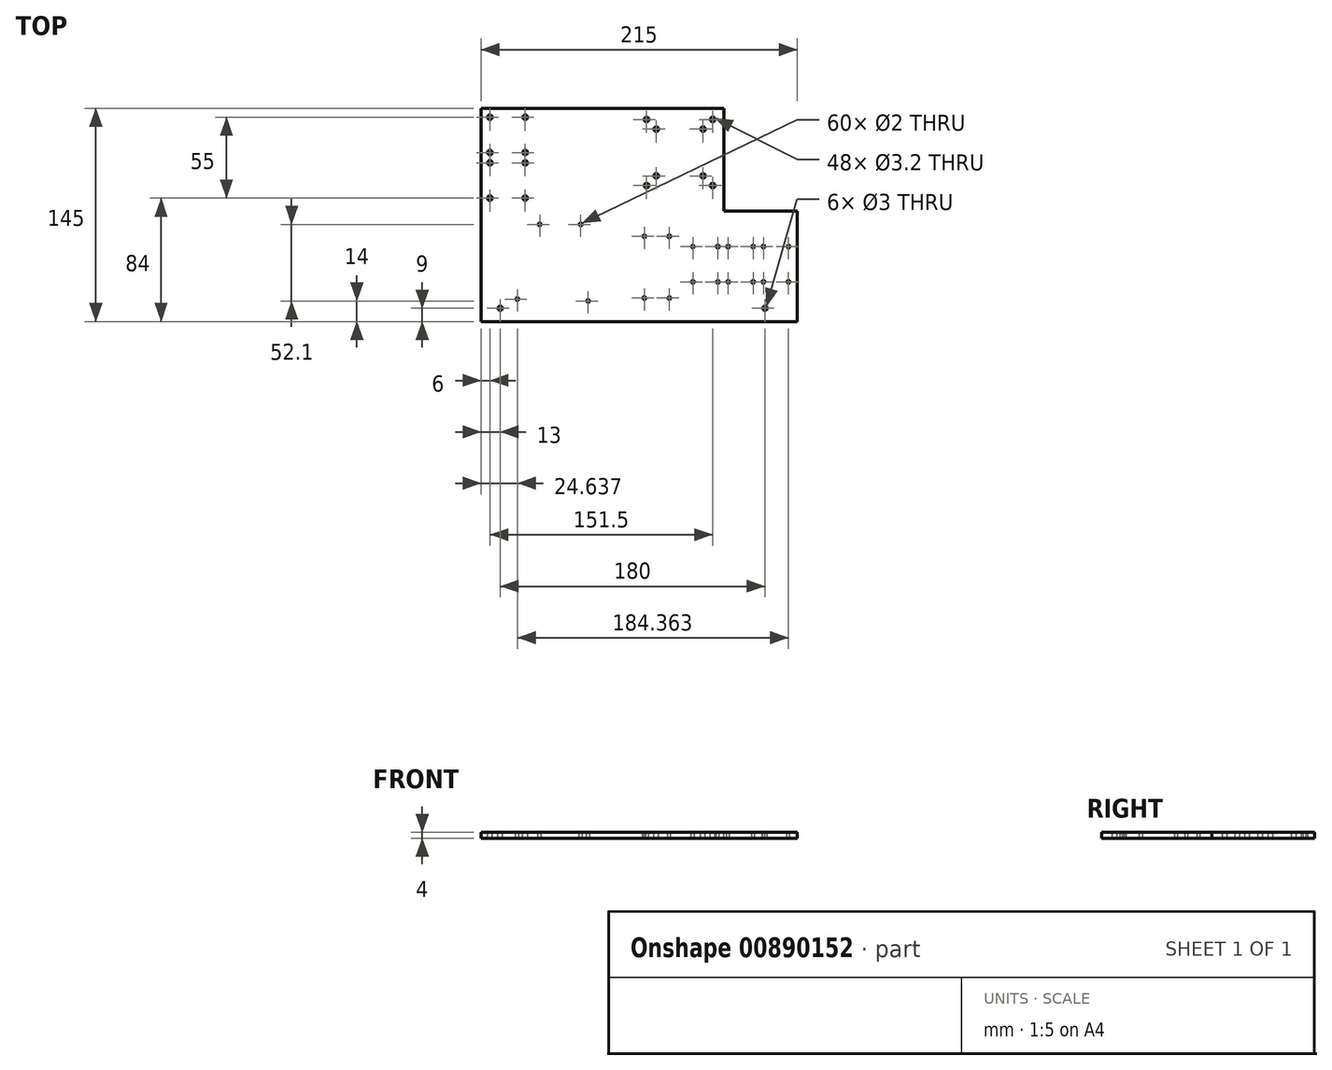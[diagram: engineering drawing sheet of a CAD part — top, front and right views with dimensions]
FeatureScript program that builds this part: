
annotation { "Feature Type Name" : "Feature", "Feature Type Description" : "" }
export const myFeature = defineFeature(function(context is Context, id is Id, definition is map)
    precondition{}
    {
        {
            var Q0;
            Q0=qCreatedBy(makeId("Top.planeOp"),FACE);
            var sketch = newSketch(context, id + "F0", { "sketchPlane" : qUnion([Q0])});
            skLineSegment(sketch, "E0.bottom", {"start": v(-107.5, 72.5) * mm, "end": v(107.5, 72.5) * mm});
            skLineSegment(sketch, "E0.top", {"start": v(-107.5, -72.5) * mm, "end": v(107.5, -72.5) * mm});
            skLineSegment(sketch, "E0.left", {"start": v(-107.5, 72.5) * mm, "end": v(-107.5, -72.5) * mm});
            skLineSegment(sketch, "E0.right", {"start": v(107.5, 72.5) * mm, "end": v(107.5, -72.5) * mm});
            skSolve(sketch);
        }
        {
            var Q0;
            Q0 = qSketchRegion(id + "F0", true);
            extrude(context, id + "F1", {"entities" : qUnion([Q0]), "depth" : 4 * mm, "offsetDistance" : 25 * mm});
        }
        {
            var Q0;
            Q0=makeQuery(id+"F1.opExtrude","CAP_FACE",FACE,{"disambiguationData":[OSD([sQuery(id+"F0.wireOp",EDGE,"E0.bottom"),sQuery(id+"F0.wireOp",EDGE,"E0.top"),sQuery(id+"F0.wireOp",EDGE,"E0.left"),sQuery(id+"F0.wireOp",EDGE,"E0.right")])],"isStart":false});
            var sketch = newSketch(context, id + "F2", { "sketchPlane" : qUnion([Q0])});
            skLineSegment(sketch, "E1", {"start": v(-112.37, -63.5) * mm, "end": v(127.47, -63.5) * mm, "construction": true});
            skCircle(sketch, "E2", {"center": v(-94.5, -63.5) * mm, "radius": 1.5 * mm});
            skCircle(sketch, "E3", {"center": v(85.5, -63.5) * mm, "radius": 1.5 * mm});
            skSolve(sketch);
        }
        {
            var Q0;
            Q0 = qSketchRegion(id + "F2", true);
            extrude(context, id + "F3", {"entities" : qUnion([Q0]), "operationType" : NewBodyOperationType.REMOVE, "endBound" : BoundingType.THROUGH_ALL, "oppositeDirection" : true, "depth" : 25 * mm, "offsetDistance" : 25 * mm});
        }
        {
            var Q0;
            Q0=makeQuery(id+"F1.opExtrude","CAP_FACE",FACE,{"disambiguationData":[OSD([sQuery(id+"F0.wireOp",EDGE,"E0.bottom"),sQuery(id+"F0.wireOp",EDGE,"E0.top"),sQuery(id+"F0.wireOp",EDGE,"E0.left"),sQuery(id+"F0.wireOp",EDGE,"E0.right")])],"isStart":false});
            var sketch = newSketch(context, id + "F4", { "sketchPlane" : qUnion([Q0])});
            skLineSegment(sketch, "E4.bottom", {"start": v(107.5, 72.5) * mm, "end": v(57.5, 72.5) * mm});
            skLineSegment(sketch, "E4.top", {"start": v(107.5, 2.5) * mm, "end": v(57.5, 2.5) * mm});
            skLineSegment(sketch, "E4.left", {"start": v(107.5, 72.5) * mm, "end": v(107.5, 2.5) * mm});
            skLineSegment(sketch, "E4.right", {"start": v(57.5, 72.5) * mm, "end": v(57.5, 2.5) * mm});
            skSolve(sketch);
        }
        {
            var Q0;
            Q0 = qSketchRegion(id + "F4", true);
            extrude(context, id + "F5", {"entities" : qUnion([Q0]), "operationType" : NewBodyOperationType.REMOVE, "endBound" : BoundingType.THROUGH_ALL, "oppositeDirection" : true, "depth" : 25 * mm, "offsetDistance" : 25 * mm});
        }
        {
            var Q0;
            Q0=makeQuery(id+"F1.opExtrude","CAP_FACE",FACE,{"disambiguationData":[OSD([sQuery(id+"F0.wireOp",EDGE,"E0.bottom"),sQuery(id+"F0.wireOp",EDGE,"E0.top"),sQuery(id+"F0.wireOp",EDGE,"E0.left"),sQuery(id+"F0.wireOp",EDGE,"E0.right")])],"isStart":false});
            var sketch = newSketch(context, id + "F6", { "sketchPlane" : qUnion([Q0])});
            skLineSegment(sketch, "E5.bottom", {"start": v(-101.5, 66.5) * mm, "end": v(-77.5, 66.5) * mm, "construction": true});
            skLineSegment(sketch, "E5.top", {"start": v(-101.5, 42.5) * mm, "end": v(-77.5, 42.5) * mm, "construction": true});
            skLineSegment(sketch, "E5.left", {"start": v(-101.5, 66.5) * mm, "end": v(-101.5, 42.5) * mm, "construction": true});
            skLineSegment(sketch, "E5.right", {"start": v(-77.5, 66.5) * mm, "end": v(-77.5, 42.5) * mm, "construction": true});
            skCircle(sketch, "E6", {"center": v(-101.5, 66.5) * mm, "radius": 1.6 * mm});
            skCircle(sketch, "E7", {"center": v(-77.5, 66.5) * mm, "radius": 1.6 * mm});
            skCircle(sketch, "E8", {"center": v(-77.5, 42.5) * mm, "radius": 1.6 * mm});
            skCircle(sketch, "E9", {"center": v(-101.5, 42.5) * mm, "radius": 1.6 * mm});
            skLineSegment(sketch, "E10.bottom", {"start": v(-101.5, 35.5) * mm, "end": v(-77.5, 35.5) * mm, "construction": true});
            skLineSegment(sketch, "E10.top", {"start": v(-101.5, 11.5) * mm, "end": v(-77.5, 11.5) * mm, "construction": true});
            skLineSegment(sketch, "E10.left", {"start": v(-101.5, 35.5) * mm, "end": v(-101.5, 11.5) * mm, "construction": true});
            skLineSegment(sketch, "E10.right", {"start": v(-77.5, 35.5) * mm, "end": v(-77.5, 11.5) * mm, "construction": true});
            skCircle(sketch, "E11", {"center": v(-101.5, 35.5) * mm, "radius": 1.6 * mm});
            skCircle(sketch, "E12", {"center": v(-77.5, 35.5) * mm, "radius": 1.6 * mm});
            skCircle(sketch, "E13", {"center": v(-77.5, 11.5) * mm, "radius": 1.6 * mm});
            skCircle(sketch, "E14", {"center": v(-101.5, 11.5) * mm, "radius": 1.6 * mm});
            skLineSegment(sketch, "E15.bottom", {"start": v(101.5, -21.5) * mm, "end": v(84.5, -21.5) * mm, "construction": true});
            skLineSegment(sketch, "E15.top", {"start": v(101.5, -45.5) * mm, "end": v(84.5, -45.5) * mm, "construction": true});
            skLineSegment(sketch, "E15.left", {"start": v(101.5, -21.5) * mm, "end": v(101.5, -45.5) * mm, "construction": true});
            skLineSegment(sketch, "E15.right", {"start": v(84.5, -21.5) * mm, "end": v(84.5, -45.5) * mm, "construction": true});
            skCircle(sketch, "E16", {"center": v(101.5, -21.5) * mm, "radius": 1 * mm});
            skCircle(sketch, "E17", {"center": v(84.5, -21.5) * mm, "radius": 1 * mm});
            skCircle(sketch, "E18", {"center": v(101.5, -45.5) * mm, "radius": 1 * mm});
            skCircle(sketch, "E19", {"center": v(84.5, -45.5) * mm, "radius": 1 * mm});
            skLineSegment(sketch, "E20.bottom", {"start": v(77.5, -21.5) * mm, "end": v(60.5, -21.5) * mm, "construction": true});
            skLineSegment(sketch, "E20.top", {"start": v(77.5, -45.5) * mm, "end": v(60.5, -45.5) * mm, "construction": true});
            skLineSegment(sketch, "E20.left", {"start": v(77.5, -21.5) * mm, "end": v(77.5, -45.5) * mm, "construction": true});
            skLineSegment(sketch, "E20.right", {"start": v(60.5, -21.5) * mm, "end": v(60.5, -45.5) * mm, "construction": true});
            skCircle(sketch, "E21", {"center": v(77.5, -21.5) * mm, "radius": 1 * mm});
            skCircle(sketch, "E22", {"center": v(60.5, -21.5) * mm, "radius": 1 * mm});
            skCircle(sketch, "E23", {"center": v(77.5, -45.5) * mm, "radius": 1 * mm});
            skCircle(sketch, "E24", {"center": v(60.5, -45.5) * mm, "radius": 1 * mm});
            skLineSegment(sketch, "E25.bottom", {"start": v(53.5, -21.5) * mm, "end": v(36.5, -21.5) * mm, "construction": true});
            skLineSegment(sketch, "E25.top", {"start": v(53.5, -45.5) * mm, "end": v(36.5, -45.5) * mm, "construction": true});
            skLineSegment(sketch, "E25.left", {"start": v(53.5, -21.5) * mm, "end": v(53.5, -45.5) * mm, "construction": true});
            skLineSegment(sketch, "E25.right", {"start": v(36.5, -21.5) * mm, "end": v(36.5, -45.5) * mm, "construction": true});
            skCircle(sketch, "E26", {"center": v(53.5, -21.5) * mm, "radius": 1 * mm});
            skCircle(sketch, "E27", {"center": v(36.5, -21.5) * mm, "radius": 1 * mm});
            skCircle(sketch, "E28", {"center": v(53.5, -45.5) * mm, "radius": 1 * mm});
            skCircle(sketch, "E29", {"center": v(36.5, -45.5) * mm, "radius": 1 * mm});
            skLineSegment(sketch, "E30.bottom", {"start": v(11.6, 58.4) * mm, "end": v(43.41, 58.4) * mm, "construction": true});
            skLineSegment(sketch, "E30.top", {"start": v(11.6, 26.59) * mm, "end": v(43.41, 26.59) * mm, "construction": true});
            skLineSegment(sketch, "E30.left", {"start": v(11.6, 58.4) * mm, "end": v(11.6, 26.59) * mm, "construction": true});
            skLineSegment(sketch, "E30.right", {"start": v(43.41, 58.4) * mm, "end": v(43.41, 26.59) * mm, "construction": true});
            skLineSegment(sketch, "E31.bottom", {"start": v(5, 65) * mm, "end": v(50, 65) * mm, "construction": true});
            skLineSegment(sketch, "E31.top", {"start": v(5, 20) * mm, "end": v(50, 20) * mm, "construction": true});
            skLineSegment(sketch, "E31.left", {"start": v(5, 65) * mm, "end": v(5, 20) * mm, "construction": true});
            skLineSegment(sketch, "E31.right", {"start": v(50, 65) * mm, "end": v(50, 20) * mm, "construction": true});
            skLineSegment(sketch, "E32", {"start": v(27.5, 66.27) * mm, "end": v(27.5, -5.5) * mm, "construction": true});
            skLineSegment(sketch, "E33", {"start": v(-10.59, 42.5) * mm, "end": v(51.58, 42.5) * mm, "construction": true});
            skCircle(sketch, "E34", {"center": v(43.41, 58.4) * mm, "radius": 1.6 * mm});
            skCircle(sketch, "E35", {"center": v(11.6, 58.4) * mm, "radius": 1.6 * mm});
            skCircle(sketch, "E36", {"center": v(5, 65) * mm, "radius": 1.6 * mm});
            skCircle(sketch, "E37", {"center": v(50, 65) * mm, "radius": 1.6 * mm});
            skCircle(sketch, "E38", {"center": v(50, 20) * mm, "radius": 1.6 * mm});
            skCircle(sketch, "E39", {"center": v(43.41, 26.59) * mm, "radius": 1.6 * mm});
            skCircle(sketch, "E40", {"center": v(11.6, 26.59) * mm, "radius": 1.6 * mm});
            skCircle(sketch, "E41", {"center": v(5, 20) * mm, "radius": 1.6 * mm});
            skLineSegment(sketch, "E42.bottom", {"start": v(3.5, -14.5) * mm, "end": v(20.5, -14.5) * mm, "construction": true});
            skLineSegment(sketch, "E42.top", {"start": v(3.5, -56.5) * mm, "end": v(20.5, -56.5) * mm, "construction": true});
            skLineSegment(sketch, "E42.left", {"start": v(3.5, -14.5) * mm, "end": v(3.5, -56.5) * mm, "construction": true});
            skLineSegment(sketch, "E42.right", {"start": v(20.5, -14.5) * mm, "end": v(20.5, -56.5) * mm, "construction": true});
            skCircle(sketch, "E43", {"center": v(3.5, -14.5) * mm, "radius": 1 * mm});
            skCircle(sketch, "E44", {"center": v(20.5, -14.5) * mm, "radius": 1 * mm});
            skCircle(sketch, "E45", {"center": v(3.5, -56.5) * mm, "radius": 1 * mm});
            skCircle(sketch, "E46", {"center": v(20.5, -56.5) * mm, "radius": 1 * mm});
            skCircle(sketch, "E47", {"center": v(-82.86, -57.2) * mm, "radius": 1 * mm});
            skCircle(sketch, "E48", {"center": v(-34.66, -58.5) * mm, "radius": 1 * mm});
            skCircle(sketch, "E49", {"center": v(-39.76, -6.4) * mm, "radius": 1 * mm});
            skCircle(sketch, "E50", {"center": v(-67.66, -6.4) * mm, "radius": 1 * mm});
            skLineSegment(sketch, "E51", {"start": v(-72.84, -6.4) * mm, "end": v(-30.62, -6.4) * mm, "construction": true});
            skSolve(sketch);
        }
        {
            var Q0;
            Q0 = qSketchRegion(id + "F6", true);
            extrude(context, id + "F7", {"entities" : qUnion([Q0]), "operationType" : NewBodyOperationType.REMOVE, "endBound" : BoundingType.THROUGH_ALL, "oppositeDirection" : true, "depth" : 25 * mm, "offsetDistance" : 25 * mm});
        }
    });
